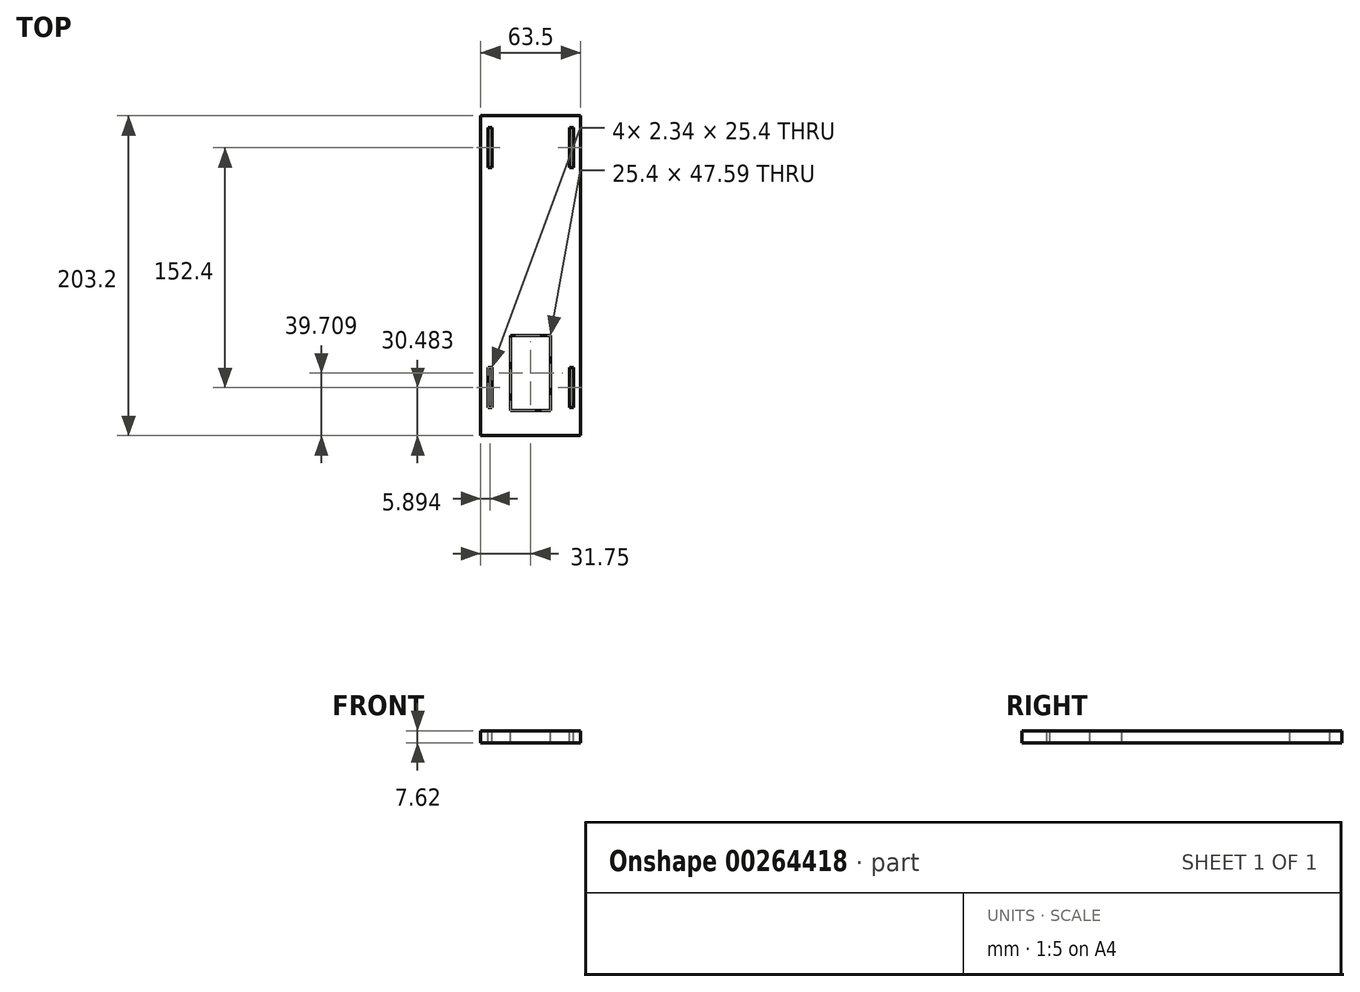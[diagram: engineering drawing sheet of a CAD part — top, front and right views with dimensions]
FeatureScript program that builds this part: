
annotation { "Feature Type Name" : "Feature", "Feature Type Description" : "" }
export const myFeature = defineFeature(function(context is Context, id is Id, definition is map)
    precondition{}
    {
        {
            var Q0;
            Q0=qCreatedBy(makeId("Top.planeOp"),FACE);
            var sketch = newSketch(context, id + "F0", { "sketchPlane" : qUnion([Q0])});
            skLineSegment(sketch, "E0", {"start": v(-63.5, -75.58) * mm, "end": v(-63.5, 127.62) * mm});
            skLineSegment(sketch, "E1", {"start": v(-63.5, 127.62) * mm, "end": v(0, 127.62) * mm});
            skLineSegment(sketch, "E2", {"start": v(0, 127.62) * mm, "end": v(0, -75.58) * mm});
            skLineSegment(sketch, "E3", {"start": v(0, -75.58) * mm, "end": v(-63.5, -75.58) * mm});
            skSolve(sketch);
        }
        {
            var Q0;
            Q0=qSketchRegion(id+"F0",true);
            extrude(context, id + "F1", {"entities" : qUnion([Q0]), "depth" : 7.62 * mm});
        }
        {
            var Q0;
            Q0=makeQuery(id+"F1.opExtrude","CAP_FACE",FACE,{"disambiguationData":[OSD([sQuery(id+"F0.wireOp",EDGE,"E0"),sQuery(id+"F0.wireOp",EDGE,"E1"),sQuery(id+"F0.wireOp",EDGE,"E2"),sQuery(id+"F0.wireOp",EDGE,"E3")])],"isStart":false});
            var sketch = newSketch(context, id + "F2", { "sketchPlane" : qUnion([Q0])});
            skLineSegment(sketch, "E4", {"start": v(-19.05, -12.08) * mm, "end": v(-44.45, -12.08) * mm});
            skLineSegment(sketch, "E5", {"start": v(-31.75, -12.08) * mm, "end": v(-44.45, -12.08) * mm});
            skLineSegment(sketch, "E6", {"start": v(-44.45, -12.08) * mm, "end": v(-44.45, -59.67) * mm});
            skLineSegment(sketch, "E7", {"start": v(-44.45, -59.67) * mm, "end": v(-44.45, -12.08) * mm});
            skLineSegment(sketch, "E8", {"start": v(-19.05, -12.08) * mm, "end": v(-19.05, -59.67) * mm});
            skLineSegment(sketch, "E9", {"start": v(-19.05, -59.67) * mm, "end": v(-44.45, -59.67) * mm});
            skPoint(sketch, "E10.end.orphan", {"position": v(-31.75, -43.83) * mm});
            skPoint(sketch, "E11.start.orphan", {"position": v(-31.75, -75.58) * mm});
            skPoint(sketch, "E12.orphan", {"position": v(0, -12.08) * mm});
            skPoint(sketch, "E13.start.orphan", {"position": v(-63.5, -12.08) * mm});
            skPoint(sketch, "E14.orphan", {"position": v(-63.5, -75.58) * mm});
            skPoint(sketch, "E15.end.orphan", {"position": v(0, -75.58) * mm});
            skSolve(sketch);
        }
        {
            var Q0;
            Q0=qSketchRegion(id+"F2",true);
            extrude(context, id + "F3", {"entities" : qUnion([Q0]), "operationType" : NewBodyOperationType.REMOVE, "oppositeDirection" : true, "depth" : 12.7 * mm});
        }
        {
            var Q0;
            Q0=makeQuery(id+"F1.opExtrude","CAP_FACE",FACE,{"disambiguationData":[OSD([sQuery(id+"F0.wireOp",EDGE,"E0"),sQuery(id+"F0.wireOp",EDGE,"E1"),sQuery(id+"F0.wireOp",EDGE,"E2"),sQuery(id+"F0.wireOp",EDGE,"E3")])],"isStart":false});
            var sketch = newSketch(context, id + "F4", { "sketchPlane" : qUnion([Q0])});
            skLineSegment(sketch, "E16.bottom", {"start": v(-58.77, 120) * mm, "end": v(-56.44, 120) * mm});
            skLineSegment(sketch, "E16.top", {"start": v(-58.77, 94.6) * mm, "end": v(-56.44, 94.6) * mm});
            skLineSegment(sketch, "E16.left", {"start": v(-58.77, 120) * mm, "end": v(-58.77, 94.6) * mm});
            skLineSegment(sketch, "E16.right", {"start": v(-56.44, 120) * mm, "end": v(-56.44, 94.6) * mm});
            skLineSegment(sketch, "E17.bottom", {"start": v(-58.78, -57.8) * mm, "end": v(-56.44, -57.8) * mm});
            skLineSegment(sketch, "E17.top", {"start": v(-58.78, -32.4) * mm, "end": v(-56.44, -32.4) * mm});
            skLineSegment(sketch, "E17.left", {"start": v(-58.78, -57.8) * mm, "end": v(-58.78, -32.4) * mm});
            skLineSegment(sketch, "E17.right", {"start": v(-56.44, -57.8) * mm, "end": v(-56.44, -32.4) * mm});
            skLineSegment(sketch, "E18", {"start": v(-31.75, 127.62) * mm, "end": v(-31.75, 42) * mm, "construction": true});
            skLineSegment(sketch, "E19.MirrorCS", {"start": v(-7.06, 120) * mm, "end": v(-7.06, 94.6) * mm});
            skLineSegment(sketch, "E20.MirrorCS", {"start": v(-4.73, 94.6) * mm, "end": v(-7.06, 94.6) * mm});
            skLineSegment(sketch, "E21.MirrorCS", {"start": v(-4.73, 120) * mm, "end": v(-4.73, 94.6) * mm});
            skLineSegment(sketch, "E22.MirrorCS", {"start": v(-4.73, 120) * mm, "end": v(-7.06, 120) * mm});
            skLineSegment(sketch, "E23.MirrorCS", {"start": v(-4.72, -57.8) * mm, "end": v(-7.06, -57.8) * mm});
            skLineSegment(sketch, "E24.MirrorCS", {"start": v(-7.06, -57.8) * mm, "end": v(-7.06, -32.4) * mm});
            skLineSegment(sketch, "E25.MirrorCS", {"start": v(-4.72, -32.4) * mm, "end": v(-7.06, -32.4) * mm});
            skLineSegment(sketch, "E26.MirrorCS", {"start": v(-4.72, -57.8) * mm, "end": v(-4.72, -32.4) * mm});
            skSolve(sketch);
        }
        {
            var Q0;
            Q0=qSketchRegion(id+"F4",true);
            extrude(context, id + "F5", {"entities" : qUnion([Q0]), "operationType" : NewBodyOperationType.REMOVE, "oppositeDirection" : true, "depth" : 25.4 * mm});
        }
    });
